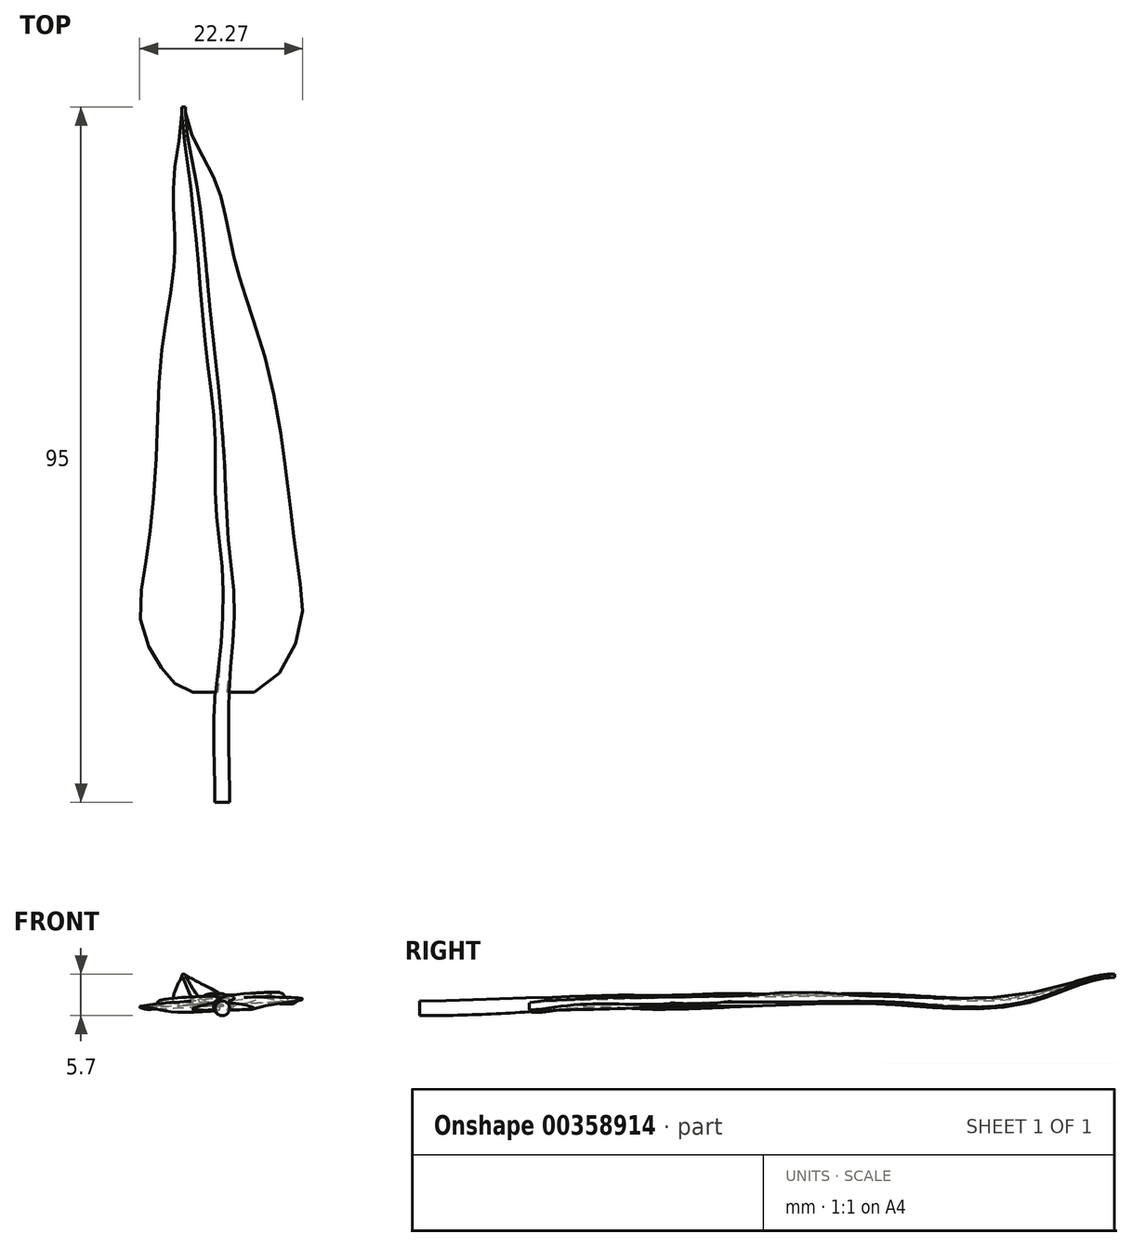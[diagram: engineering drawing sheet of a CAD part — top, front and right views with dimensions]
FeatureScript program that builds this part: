
annotation { "Feature Type Name" : "Feature", "Feature Type Description" : "" }
export const myFeature = defineFeature(function(context is Context, id is Id, definition is map)
    precondition{}
    {
        {
            var Q0;
            Q0=qCreatedBy(makeId("Front.planeOp"),FACE);
            var sketch = newSketch(context, id + "F0", { "sketchPlane" : qUnion([Q0])});
            skCircle(sketch, "E0", {"center": v(0, 0) * mm, "radius": 1 * mm});
            skSolve(sketch);
        }
        {
            var Q0;
            Q0=qCreatedBy(makeId("Front.planeOp"),FACE);
            cPlane(context, id + "F1", {"entities" : qUnion([Q0]), "cplaneType" : CPlaneType.OFFSET, "offset" : 15 * mm, "oppositeDirection" : true, "width" : 150 * mm, "height" : 150 * mm});
        }
        {
            var Q0;
            Q0=qCreatedBy(id+"F1.planeOp",FACE);
            var sketch = newSketch(context, id + "F2", { "sketchPlane" : qUnion([Q0])});
            skCircle(sketch, "E1", {"center": v(0, 0.48) * mm, "radius": 0.95 * mm});
            skSolve(sketch);
        }
        {
            var Q0;
            Q0=qCreatedBy(id+"F1.planeOp",FACE);
            cPlane(context, id + "F3", {"entities" : qUnion([Q0]), "cplaneType" : CPlaneType.OFFSET, "offset" : 5 * mm, "oppositeDirection" : true, "width" : 150 * mm, "height" : 150 * mm});
        }
        {
            var Q0;
            Q0=qCreatedBy(id+"F3.planeOp",FACE);
            var sketch = newSketch(context, id + "F4", { "sketchPlane" : qUnion([Q0])});
            skCircle(sketch, "E2", {"center": v(0.5, 0.7) * mm, "radius": 0.9 * mm});
            skSolve(sketch);
        }
        {
            var Q0;
            Q0=qCreatedBy(id+"F3.planeOp",FACE);
            cPlane(context, id + "F5", {"entities" : qUnion([Q0]), "cplaneType" : CPlaneType.OFFSET, "offset" : 10 * mm, "oppositeDirection" : true, "width" : 150 * mm, "height" : 150 * mm});
        }
        {
            var Q0;
            Q0=qCreatedBy(id+"F5.planeOp",FACE);
            var sketch = newSketch(context, id + "F6", { "sketchPlane" : qUnion([Q0])});
            skCircle(sketch, "E3", {"center": v(0.8, 0.94) * mm, "radius": 0.85 * mm});
            skSolve(sketch);
        }
        {
            var Q0;
            Q0=qCreatedBy(id+"F5.planeOp",FACE);
            cPlane(context, id + "F7", {"entities" : qUnion([Q0]), "cplaneType" : CPlaneType.OFFSET, "offset" : 8 * mm, "oppositeDirection" : true, "width" : 150 * mm, "height" : 150 * mm});
        }
        {
            var Q0;
            Q0=qCreatedBy(id+"F7.planeOp",FACE);
            var sketch = newSketch(context, id + "F8", { "sketchPlane" : qUnion([Q0])});
            skCircle(sketch, "E4", {"center": v(0, 1.13) * mm, "radius": 0.8 * mm});
            skSolve(sketch);
        }
        {
            var Q0;
            Q0=qCreatedBy(id+"F7.planeOp",FACE);
            cPlane(context, id + "F9", {"entities" : qUnion([Q0]), "cplaneType" : CPlaneType.OFFSET, "offset" : 11 * mm, "oppositeDirection" : true, "width" : 150 * mm, "height" : 150 * mm});
        }
        {
            var Q0;
            Q0=qCreatedBy(id+"F9.planeOp",FACE);
            var sketch = newSketch(context, id + "F10", { "sketchPlane" : qUnion([Q0])});
            skCircle(sketch, "E5", {"center": v(-0.37, 1.18) * mm, "radius": 0.75 * mm});
            skSolve(sketch);
        }
        {
            var Q0;
            Q0=qCreatedBy(id+"F9.planeOp",FACE);
            cPlane(context, id + "F11", {"entities" : qUnion([Q0]), "cplaneType" : CPlaneType.OFFSET, "offset" : 15 * mm, "oppositeDirection" : true, "width" : 150 * mm, "height" : 150 * mm});
        }
        {
            var Q0;
            Q0=qCreatedBy(id+"F11.planeOp",FACE);
            var sketch = newSketch(context, id + "F12", { "sketchPlane" : qUnion([Q0])});
            skCircle(sketch, "E6", {"center": v(-1.88, 1.23) * mm, "radius": 0.7 * mm});
            skSolve(sketch);
        }
        {
            var Q0;
            Q0=qCreatedBy(id+"F11.planeOp",FACE);
            cPlane(context, id + "F13", {"entities" : qUnion([Q0]), "cplaneType" : CPlaneType.OFFSET, "offset" : 21 * mm, "oppositeDirection" : true, "width" : 150 * mm, "height" : 150 * mm});
        }
        {
            var Q0;
            Q0=qCreatedBy(id+"F13.planeOp",FACE);
            var sketch = newSketch(context, id + "F14", { "sketchPlane" : qUnion([Q0])});
            skCircle(sketch, "E7", {"center": v(-3.99, 1.77) * mm, "radius": 0.5 * mm});
            skSolve(sketch);
        }
        {
            var Q0;
            Q0=qCreatedBy(id+"F13.planeOp",FACE);
            cPlane(context, id + "F15", {"entities" : qUnion([Q0]), "cplaneType" : CPlaneType.OFFSET, "offset" : 10 * mm, "oppositeDirection" : true, "width" : 150 * mm, "height" : 150 * mm});
        }
        {
            var Q0;
            Q0=qCreatedBy(id+"F15.planeOp",FACE);
            var sketch = newSketch(context, id + "F16", { "sketchPlane" : qUnion([Q0])});
            skCircle(sketch, "E8", {"center": v(-5.29, 4.45) * mm, "radius": 0.25 * mm});
            skSolve(sketch);
        }
        {
            var Q0;
            Q0 = qSketchRegion(id + "F0", true);
            var Q1;
            Q1 = qSketchRegion(id + "F2", true);
            var Q2;
            Q2 = qSketchRegion(id + "F4", true);
            var Q3;
            Q3 = qSketchRegion(id + "F6", true);
            var Q4;
            Q4 = qSketchRegion(id + "F8", true);
            var Q5;
            Q5 = qSketchRegion(id + "F10", true);
            var Q6;
            Q6 = qSketchRegion(id + "F12", true);
            var Q7;
            Q7 = qSketchRegion(id + "F14", true);
            var Q8;
            Q8 = qSketchRegion(id + "F16", true);
            loft(context, id + "F17", {"startCondition" : LoftEndDerivativeType.NORMAL_TO_PROFILE, "startMagnitude" : 1, "endCondition" : LoftEndDerivativeType.NORMAL_TO_PROFILE, "endMagnitude" : 1, "sheetProfilesArray" : [{ "sheetProfileEntities" : qUnion([Q0]) }, { "sheetProfileEntities" : qUnion([Q1]) }, { "sheetProfileEntities" : qUnion([Q2]) }, { "sheetProfileEntities" : qUnion([Q3]) }, { "sheetProfileEntities" : qUnion([Q4]) }, { "sheetProfileEntities" : qUnion([Q5]) }, { "sheetProfileEntities" : qUnion([Q6]) }, { "sheetProfileEntities" : qUnion([Q7]) }, { "sheetProfileEntities" : qUnion([Q8]) }]});
        }
        {
            var Q0;
            Q0=qCreatedBy(id+"F1.planeOp",FACE);
            var sketch = newSketch(context, id + "F18", { "sketchPlane" : qUnion([Q0])});
            skFitSpline(sketch, "E9", {"points": [v(0, 0.77) * mm, v(4.35, 0) * mm, v(0, -0.2) * mm, v(-4.02, -0.12) * mm, v(0, 0.77) * mm]});
            skSolve(sketch);
        }
        {
            var Q0;
            Q0=qCreatedBy(id+"F3.planeOp",FACE);
            var sketch = newSketch(context, id + "F19", { "sketchPlane" : qUnion([Q0])});
            skFitSpline(sketch, "E10", {"points": [v(0.49, 1.12) * mm, v(9.23, 0.92) * mm, v(0.57, 0.32) * mm, v(-9.4, 0) * mm, v(0.49, 1.12) * mm]});
            skSolve(sketch);
        }
        {
            var Q0;
            Q0=qCreatedBy(id+"F5.planeOp",FACE);
            var sketch = newSketch(context, id + "F20", { "sketchPlane" : qUnion([Q0])});
            skFitSpline(sketch, "E11", {"points": [v(0.79, 1.42) * mm, v(10.61, 1.24) * mm, v(0.92, 0.5) * mm, v(-10.86, 0) * mm, v(0.79, 1.42) * mm]});
            skSolve(sketch);
        }
        {
            var Q0;
            Q0=qCreatedBy(id+"F7.planeOp",FACE);
            var sketch = newSketch(context, id + "F21", { "sketchPlane" : qUnion([Q0])});
            skFitSpline(sketch, "E12", {"points": [v(0, 1.57) * mm, v(9.56, 0.64) * mm, v(0, 0.8) * mm, v(-9.74, 0) * mm, v(0, 1.57) * mm]});
            skSolve(sketch);
        }
        {
            var Q0;
            Q0=qCreatedBy(id+"F9.planeOp",FACE);
            var sketch = newSketch(context, id + "F22", { "sketchPlane" : qUnion([Q0])});
            skFitSpline(sketch, "E13", {"points": [v(-0.37, 1.7) * mm, v(8.2, 2) * mm, v(-0.24, 0.8) * mm, v(-8.95, 0.6) * mm, v(-0.37, 1.7) * mm]});
            skSolve(sketch);
        }
        {
            var Q0;
            Q0=qCreatedBy(id+"F11.planeOp",FACE);
            var sketch = newSketch(context, id + "F23", { "sketchPlane" : qUnion([Q0])});
            skFitSpline(sketch, "E14", {"points": [v(-1.94, 1.6) * mm, v(4.87, 1.24) * mm, v(-1.83, 0.88) * mm, v(-7.98, 1.03) * mm, v(-1.94, 1.6) * mm]});
            skSolve(sketch);
        }
        {
            var Q0;
            Q0=qCreatedBy(id+"F13.planeOp",FACE);
            var sketch = newSketch(context, id + "F24", { "sketchPlane" : qUnion([Q0])});
            skFitSpline(sketch, "E15", {"points": [v(-3.94, 2.04) * mm, v(-1.02, 2.38) * mm, v(-3.98, 1.52) * mm, v(-6.65, 1.8) * mm, v(-3.94, 2.04) * mm]});
            skSolve(sketch);
        }
        {
            var Q0;
            Q0=qCreatedBy(id+"F15.planeOp",FACE);
            var sketch = newSketch(context, id + "F25", { "sketchPlane" : qUnion([Q0])});
            skFitSpline(sketch, "E16", {"points": [v(-5.3, 4.58) * mm, v(-5.07, 4.52) * mm, v(-5.24, 4.35) * mm, v(-5.5, 4.35) * mm, v(-5.3, 4.58) * mm]});
            skSolve(sketch);
        }
        {
            var Q1;
            Q1 = qSketchRegion(id + "F18", true);
            var Q2;
            Q2 = qSketchRegion(id + "F19", true);
            var Q3;
            Q3 = qSketchRegion(id + "F20", true);
            var Q4;
            Q4 = qSketchRegion(id + "F21", true);
            var Q5;
            Q5 = qSketchRegion(id + "F22", true);
            var Q6;
            Q6 = qSketchRegion(id + "F23", true);
            var Q7;
            Q7 = qSketchRegion(id + "F24", true);
            var Q8;
            Q8 = qSketchRegion(id + "F25", true);
            loft(context, id + "F26", {"operationType" : NewBodyOperationType.ADD, "startCondition" : LoftEndDerivativeType.TANGENT_TO_PROFILE, "startMagnitude" : 1, "endCondition" : LoftEndDerivativeType.NORMAL_TO_PROFILE, "endMagnitude" : 1, "sheetProfilesArray" : [{ "sheetProfileEntities" : qUnion([Q1]) }, { "sheetProfileEntities" : qUnion([Q2]) }, { "sheetProfileEntities" : qUnion([Q3]) }, { "sheetProfileEntities" : qUnion([Q4]) }, { "sheetProfileEntities" : qUnion([Q5]) }, { "sheetProfileEntities" : qUnion([Q6]) }, { "sheetProfileEntities" : qUnion([Q7]) }, { "sheetProfileEntities" : qUnion([Q8]) }]});
        }
    });
